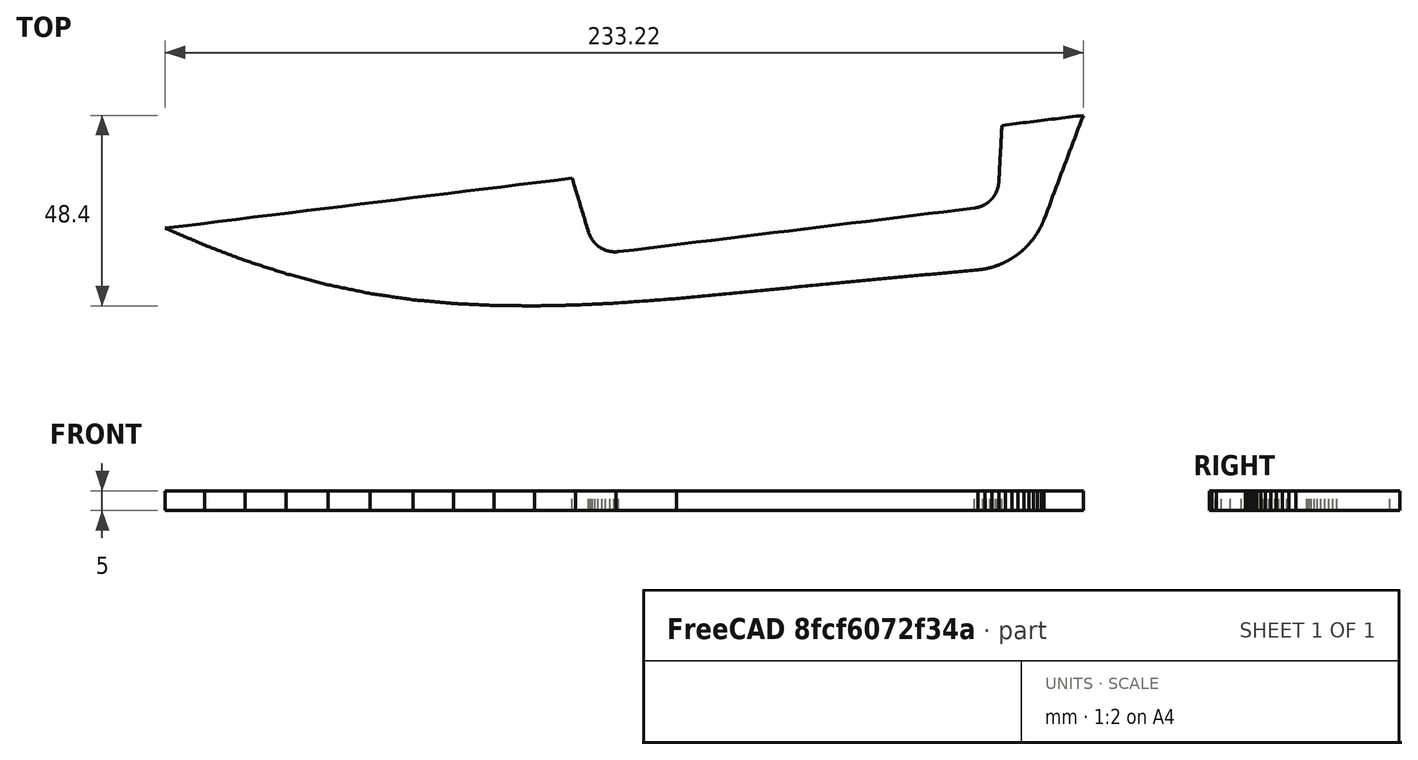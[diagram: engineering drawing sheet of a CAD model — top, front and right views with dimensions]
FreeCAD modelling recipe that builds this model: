
FCSTD DOCUMENT  (FreeCAD 0.19R)
Label: F-35_v2_parts_6
License: All rights reserved
LicenseURL: http://en.wikipedia.org/wiki/All_rights_reserved
objects: App::DocumentObjectGroup×2, PartDesign::CoordinateSystem×2, App::FeaturePython×1, Sketcher::SketchObject×1, PartDesign::Pad×1, PartDesign::Body×1, App::Part×1
note: 6 computed .brp shape members not serialized (recipe doc carries the construction recipe); baked Part::Feature solids carry a one-line shape summary decoded from their .brp

FEATURE [App::DocumentObjectGroup] Parts
FEATURE [PartDesign::CoordinateSystem] LCS_Origin
  AttacherType = Attacher::AttachEngine3D
  MapMode = 2
  Support = -> [X_Axis]
FEATURE [App::DocumentObjectGroup] Constraints
FEATURE [App::FeaturePython] Variables  # WARN: FeaturePython — macro-defined, semantics opaque (R4)
FEATURE [Sketcher::SketchObject] Sketch005
  FullyConstrained = false
  sketch-geometry (53):
    g0: BSplineCurve PolesCount=2 KnotsCount=2 Degree=1 IsPeriodic=0
    g1: BSplineCurve PolesCount=2 KnotsCount=2 Degree=1 IsPeriodic=0
    g2: BSplineCurve PolesCount=2 KnotsCount=2 Degree=1 IsPeriodic=0
    g3: BSplineCurve PolesCount=2 KnotsCount=2 Degree=1 IsPeriodic=0
    g4: BSplineCurve PolesCount=2 KnotsCount=2 Degree=1 IsPeriodic=0
    g5: BSplineCurve PolesCount=2 KnotsCount=2 Degree=1 IsPeriodic=0
    g6: BSplineCurve PolesCount=2 KnotsCount=2 Degree=1 IsPeriodic=0
    g7: BSplineCurve PolesCount=2 KnotsCount=2 Degree=1 IsPeriodic=0
    g8: BSplineCurve PolesCount=2 KnotsCount=2 Degree=1 IsPeriodic=0
    g9: BSplineCurve PolesCount=2 KnotsCount=2 Degree=1 IsPeriodic=0
    g10: BSplineCurve PolesCount=2 KnotsCount=2 Degree=1 IsPeriodic=0
    g11: BSplineCurve PolesCount=2 KnotsCount=2 Degree=1 IsPeriodic=0
    g12: BSplineCurve PolesCount=2 KnotsCount=2 Degree=1 IsPeriodic=0
    g13: BSplineCurve PolesCount=2 KnotsCount=2 Degree=1 IsPeriodic=0
    g14: BSplineCurve PolesCount=2 KnotsCount=2 Degree=1 IsPeriodic=0
    g15: BSplineCurve PolesCount=2 KnotsCount=2 Degree=1 IsPeriodic=0
    g16: BSplineCurve PolesCount=2 KnotsCount=2 Degree=1 IsPeriodic=0
    g17: BSplineCurve PolesCount=2 KnotsCount=2 Degree=1 IsPeriodic=0
    g18: BSplineCurve PolesCount=2 KnotsCount=2 Degree=1 IsPeriodic=0
    g19: BSplineCurve PolesCount=2 KnotsCount=2 Degree=1 IsPeriodic=0
    g20: BSplineCurve PolesCount=2 KnotsCount=2 Degree=1 IsPeriodic=0
    g21: BSplineCurve PolesCount=2 KnotsCount=2 Degree=1 IsPeriodic=0
    g22: BSplineCurve PolesCount=2 KnotsCount=2 Degree=1 IsPeriodic=0
    g23: BSplineCurve PolesCount=2 KnotsCount=2 Degree=1 IsPeriodic=0
    g24: BSplineCurve PolesCount=2 KnotsCount=2 Degree=1 IsPeriodic=0
    g25: BSplineCurve PolesCount=2 KnotsCount=2 Degree=1 IsPeriodic=0
    g26: BSplineCurve PolesCount=2 KnotsCount=2 Degree=1 IsPeriodic=0
    g27: BSplineCurve PolesCount=2 KnotsCount=2 Degree=1 IsPeriodic=0
    g28: BSplineCurve PolesCount=2 KnotsCount=2 Degree=1 IsPeriodic=0
    g29: BSplineCurve PolesCount=2 KnotsCount=2 Degree=1 IsPeriodic=0
    g30: BSplineCurve PolesCount=2 KnotsCount=2 Degree=1 IsPeriodic=0
    g31: BSplineCurve PolesCount=2 KnotsCount=2 Degree=1 IsPeriodic=0
    g32: BSplineCurve PolesCount=2 KnotsCount=2 Degree=1 IsPeriodic=0
    g33: BSplineCurve PolesCount=2 KnotsCount=2 Degree=1 IsPeriodic=0
    g34: BSplineCurve PolesCount=2 KnotsCount=2 Degree=1 IsPeriodic=0
    g35: BSplineCurve PolesCount=2 KnotsCount=2 Degree=1 IsPeriodic=0
    g36: BSplineCurve PolesCount=2 KnotsCount=2 Degree=1 IsPeriodic=0
    g37: BSplineCurve PolesCount=2 KnotsCount=2 Degree=1 IsPeriodic=0
    g38: BSplineCurve PolesCount=2 KnotsCount=2 Degree=1 IsPeriodic=0
    g39: BSplineCurve PolesCount=2 KnotsCount=2 Degree=1 IsPeriodic=0
    g40: BSplineCurve PolesCount=2 KnotsCount=2 Degree=1 IsPeriodic=0
    g41: BSplineCurve PolesCount=2 KnotsCount=2 Degree=1 IsPeriodic=0
    g42: BSplineCurve PolesCount=2 KnotsCount=2 Degree=1 IsPeriodic=0
    g43: BSplineCurve PolesCount=2 KnotsCount=2 Degree=1 IsPeriodic=0
    g44: BSplineCurve PolesCount=2 KnotsCount=2 Degree=1 IsPeriodic=0
    g45: BSplineCurve PolesCount=2 KnotsCount=2 Degree=1 IsPeriodic=0
    g46: BSplineCurve PolesCount=2 KnotsCount=2 Degree=1 IsPeriodic=0
    g47: BSplineCurve PolesCount=2 KnotsCount=2 Degree=1 IsPeriodic=0
    g48: BSplineCurve PolesCount=2 KnotsCount=2 Degree=1 IsPeriodic=0
    g49: BSplineCurve PolesCount=2 KnotsCount=2 Degree=1 IsPeriodic=0
    g50: BSplineCurve PolesCount=2 KnotsCount=2 Degree=1 IsPeriodic=0
    g51: BSplineCurve PolesCount=2 KnotsCount=2 Degree=1 IsPeriodic=0
    g52: BSplineCurve PolesCount=2 KnotsCount=2 Degree=1 IsPeriodic=0
  constraints (43):
    c: Coincident(g0,g1)
    c: Coincident(g1,g2)
    c: Coincident(g2,g3)
    c: Coincident(g3,g4)
    c: Coincident(g4,g5)
    c: Coincident(g5,g6)
    c: Coincident(g6,g7)
    c: Coincident(g7,g8)
    c: Coincident(g10,g11)
    c: Coincident(g11,g12)
    c: Coincident(g12,g13)
    c: Coincident(g13,g14)
    c: Coincident(g14,g15)
    c: Coincident(g15,g16)
    c: Coincident(g16,g17)
    c: Coincident(g17,g18)
    c: Coincident(g22,g23)
    c: Coincident(g23,g24)
    c: Coincident(g24,g25)
    c: Coincident(g25,g26)
    c: Coincident(g26,g27)
    c: Coincident(g27,g28)
    c: Coincident(g28,g29)
    c: Coincident(g29,g30)
    c: Coincident(g30,g31)
    c: Coincident(g31,g32)
    c: Coincident(g32,g33)
    c: Coincident(g35,g36)
    c: Coincident(g36,g37)
    c: Coincident(g37,g38)
    c: Coincident(g38,g39)
    c: Coincident(g39,g40)
    c: Coincident(g40,g41)
    c: Coincident(g41,g42)
    c: Coincident(g42,g43)
    c: Coincident(g43,g44)
    c: Coincident(g44,g45)
    c: Coincident(g45,g46)
    c: Coincident(g46,g47)
    c: Coincident(g47,g48)
    c: Coincident(g48,g49)
    c: Coincident(g49,g50)
    c: Coincident(g50,g51)
FEATURE [PartDesign::Pad] Pad005
  Direction = (1,1,1)
  Length = 5
  Length2 = 100
  Profile = -> Sketch005
  Type = 0
FEATURE [PartDesign::Body] Body005  label="Part6"
  Group = -> [Sketch005,Pad005]
  Origin = -> Origin006
  Tip = -> Pad005
FEATURE [PartDesign::CoordinateSystem] LCS_1
  AttacherType = Attacher::AttachEngine3D
  AttachmentOffset = pos=(0,0,0) rot=(0,0,-1;0.122173rad)
  MapMode = 7
  Placement = pos=(448.781,-222.831,0) rot=(-0.061049,0.998135,0;3.14159rad)
  Support = -> [Pad005]
FEATURE [App::Part] Model
  Configuration = 0
  Group = -> [LCS_Origin,Constraints,Variables,Body005,LCS_1]
  Origin = -> Origin
  Type = Assembly4 Model
